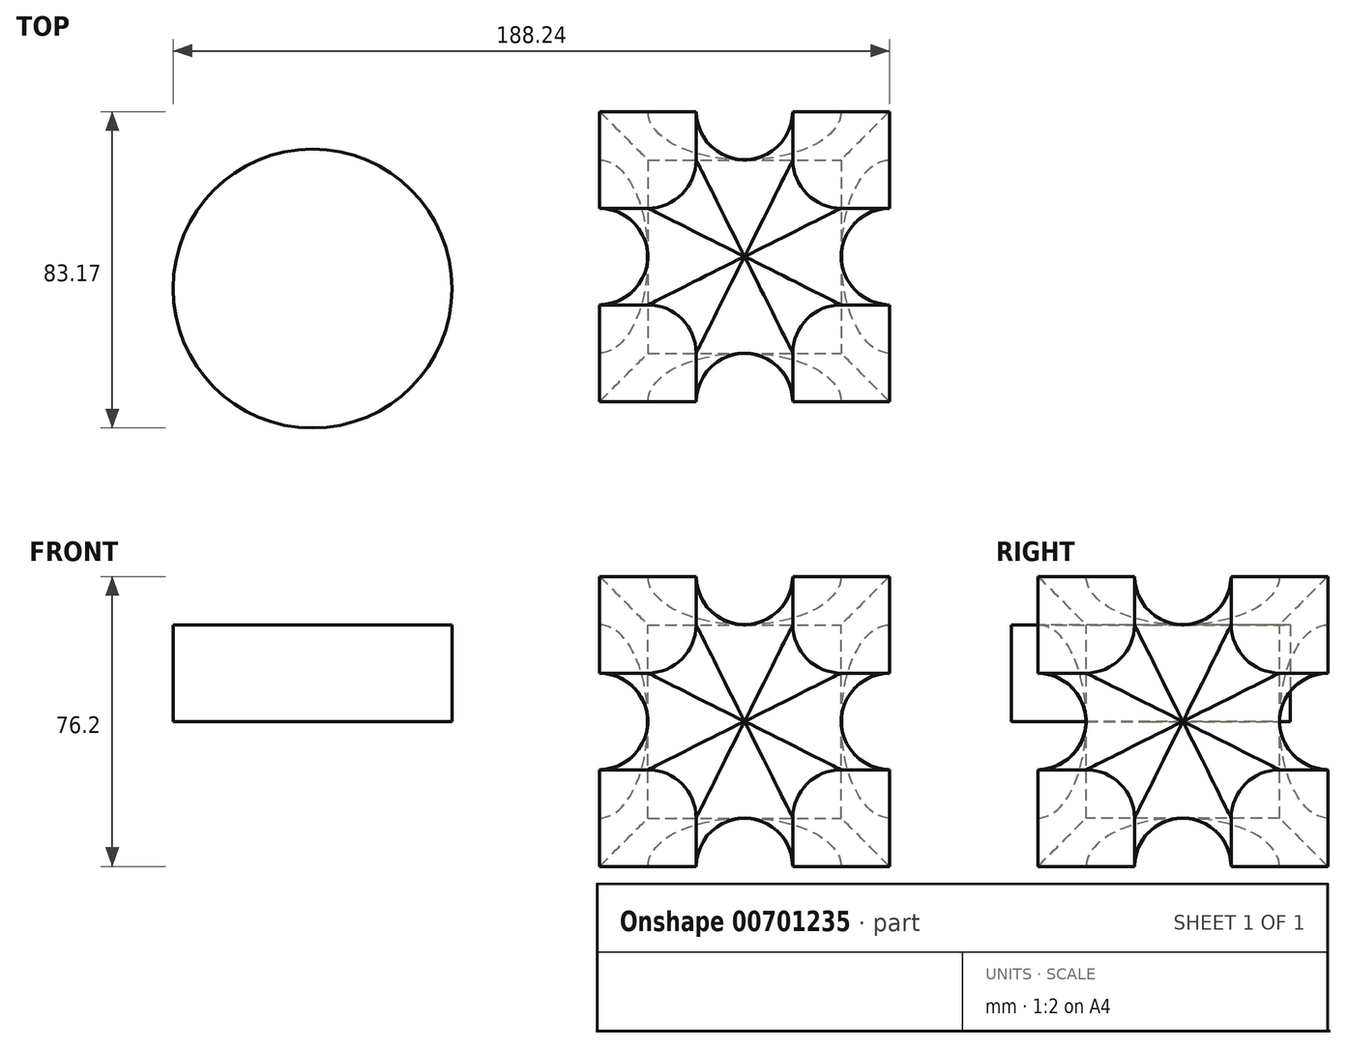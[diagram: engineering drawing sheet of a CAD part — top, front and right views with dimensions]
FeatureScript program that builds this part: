
annotation { "Feature Type Name" : "Feature", "Feature Type Description" : "" }
export const myFeature = defineFeature(function(context is Context, id is Id, definition is map)
    precondition{}
    {
        {
            var Q0;
            Q0=qCreatedBy(makeId("Top.planeOp"),FACE);
            var sketch = newSketch(context, id + "F0", { "sketchPlane" : qUnion([Q0])});
            skLineSegment(sketch, "E0.bottom", {"start": v(38.1, -38.1) * mm, "end": v(-38.1, -38.1) * mm});
            skLineSegment(sketch, "E0.top", {"start": v(38.1, 38.1) * mm, "end": v(-38.1, 38.1) * mm});
            skLineSegment(sketch, "E0.left", {"start": v(38.1, -38.1) * mm, "end": v(38.1, 38.1) * mm});
            skLineSegment(sketch, "E0.right", {"start": v(-38.1, -38.1) * mm, "end": v(-38.1, 38.1) * mm});
            skPoint(sketch, "E0.middle", {"position": v(0, 0) * mm});
            skSolve(sketch);
        }
        {
            var Q0;
            Q0 = qSketchRegion(id + "F0", true);
            extrude(context, id + "F1", {"entities" : qUnion([Q0]), "endBound" : BoundingType.SYMMETRIC, "depth" : 76.2 * mm, "offsetDistance" : 25.4 * mm});
        }
        {
            var Q0;
            Q0=makeQuery(id+"F1.opExtrude","CAP_FACE",FACE,{"disambiguationData":[OSD([sQuery(id+"F0.wireOp",EDGE,"E0.bottom"),sQuery(id+"F0.wireOp",EDGE,"E0.top"),sQuery(id+"F0.wireOp",EDGE,"E0.left"),sQuery(id+"F0.wireOp",EDGE,"E0.right")])],"isStart":false});
            var sketch = newSketch(context, id + "F2", { "sketchPlane" : qUnion([Q0])});
            skArc(sketch, "E1", {"start": v(-12.7, -38.1) * mm, "mid": v(0, -25.4) * mm, "end": v(12.7, -38.1) * mm});
            skArc(sketch, "E2", {"start": v(38.1, 12.7) * mm, "mid": v(25.4, 0) * mm, "end": v(38.1, -12.7) * mm});
            skArc(sketch, "E3", {"start": v(-12.7, 38.1) * mm, "mid": v(0, 25.4) * mm, "end": v(12.7, 38.1) * mm});
            skArc(sketch, "E4", {"start": v(-38.1, 12.7) * mm, "mid": v(-25.4, 0) * mm, "end": v(-38.1, -12.7) * mm});
            skLineSegment(sketch, "E5", {"start": v(12.7, 38.1) * mm, "end": v(-12.7, 38.1) * mm});
            skLineSegment(sketch, "E6", {"start": v(38.1, 12.7) * mm, "end": v(38.1, -12.7) * mm});
            skLineSegment(sketch, "E7", {"start": v(12.7, -38.1) * mm, "end": v(-12.7, -38.1) * mm});
            skLineSegment(sketch, "E8", {"start": v(-38.1, 12.7) * mm, "end": v(-38.1, -12.7) * mm});
            skSolve(sketch);
        }
        {
            var Q0;
            Q0=makeQuery(id+"F1.opExtrude","SWEPT_FACE",FACE,{"disambiguationData":[OSD([sQuery(id+"F0.wireOp",EDGE,"E0.bottom")])]});
            var sketch = newSketch(context, id + "F3", { "sketchPlane" : qUnion([Q0])});
            skArc(sketch, "E9", {"start": v(12.7, 38.1) * mm, "mid": v(0, 25.4) * mm, "end": v(-12.7, 38.1) * mm});
            skArc(sketch, "E10", {"start": v(38.1, 12.7) * mm, "mid": v(25.4, 0) * mm, "end": v(38.1, -12.7) * mm});
            skArc(sketch, "E11", {"start": v(12.7, -38.1) * mm, "mid": v(0, -25.4) * mm, "end": v(-12.7, -38.1) * mm});
            skArc(sketch, "E12", {"start": v(-38.1, 12.7) * mm, "mid": v(-25.4, 0) * mm, "end": v(-38.1, -12.7) * mm});
            skLineSegment(sketch, "E13", {"start": v(-12.7, 38.1) * mm, "end": v(12.7, 38.1) * mm});
            skLineSegment(sketch, "E14", {"start": v(38.1, 12.7) * mm, "end": v(38.1, -12.7) * mm});
            skLineSegment(sketch, "E15", {"start": v(12.7, -38.1) * mm, "end": v(-12.7, -38.1) * mm});
            skLineSegment(sketch, "E16", {"start": v(-38.1, -12.7) * mm, "end": v(-38.1, 12.7) * mm});
            skSolve(sketch);
        }
        {
            var Q0;
            Q0=makeQuery(id+"F1.opExtrude","SWEPT_FACE",FACE,{"disambiguationData":[OSD([sQuery(id+"F0.wireOp",EDGE,"E0.left")])]});
            var sketch = newSketch(context, id + "F4", { "sketchPlane" : qUnion([Q0])});
            skArc(sketch, "E17", {"start": v(12.7, 38.1) * mm, "mid": v(0, 25.4) * mm, "end": v(-12.7, 38.1) * mm});
            skArc(sketch, "E18", {"start": v(38.1, 12.7) * mm, "mid": v(25.4, 0) * mm, "end": v(38.1, -12.7) * mm});
            skArc(sketch, "E19", {"start": v(12.7, -38.1) * mm, "mid": v(0, -25.4) * mm, "end": v(-12.7, -38.1) * mm});
            skArc(sketch, "E20", {"start": v(-38.1, 12.7) * mm, "mid": v(-25.4, 0) * mm, "end": v(-38.1, -12.7) * mm});
            skLineSegment(sketch, "E21", {"start": v(12.7, 38.1) * mm, "end": v(-12.7, 38.1) * mm});
            skLineSegment(sketch, "E22", {"start": v(38.1, 12.7) * mm, "end": v(38.1, -12.7) * mm});
            skLineSegment(sketch, "E23", {"start": v(12.7, -38.1) * mm, "end": v(-12.7, -38.1) * mm});
            skLineSegment(sketch, "E24", {"start": v(-38.1, 12.7) * mm, "end": v(-38.1, -12.7) * mm});
            skSolve(sketch);
        }
        {
            var Q0;
            Q0 = qSketchRegion(id + "F2", true);
            extrude(context, id + "F5", {"entities" : qUnion([Q0]), "operationType" : NewBodyOperationType.REMOVE, "endBound" : BoundingType.THROUGH_ALL, "oppositeDirection" : true, "depth" : 25.4 * mm, "offsetDistance" : 25.4 * mm});
        }
        {
            var Q0;
            Q0 = qSketchRegion(id + "F3", true);
            extrude(context, id + "F6", {"entities" : qUnion([Q0]), "operationType" : NewBodyOperationType.REMOVE, "endBound" : BoundingType.THROUGH_ALL, "oppositeDirection" : true, "depth" : 25.4 * mm, "offsetDistance" : 25.4 * mm});
        }
        {
            var Q0;
            Q0 = qSketchRegion(id + "F4", true);
            extrude(context, id + "F7", {"entities" : qUnion([Q0]), "operationType" : NewBodyOperationType.REMOVE, "endBound" : BoundingType.THROUGH_ALL, "oppositeDirection" : true, "depth" : 25.4 * mm, "offsetDistance" : 25.4 * mm});
        }
        {
            var Q0;
            Q0=makeQuery(id+"F6.boolean.opBoolean","INTERSECT",EDGE,{"disambiguationData":[OD(3.0)],"derivedFrom":[makeQuery(id+"F5.boolean.opBoolean","COPY",FACE,{"derivedFrom":makeQuery(id+"F5.opExtrude","SWEPT_FACE",FACE,{"disambiguationData":[OSD([sQuery(id+"F2.wireOp",EDGE,"E2")])]})}),makeQuery(id+"F6.opExtrude","SWEPT_FACE",FACE,{"disambiguationData":[OSD([sQuery(id+"F3.wireOp",EDGE,"E10")])]})]});
            var Q1;
            Q1=makeQuery(id+"F6.boolean.opBoolean","INTERSECT",EDGE,{"disambiguationData":[OD(2.0)],"derivedFrom":[makeQuery(id+"F5.boolean.opBoolean","COPY",FACE,{"derivedFrom":makeQuery(id+"F5.opExtrude","SWEPT_FACE",FACE,{"disambiguationData":[OSD([sQuery(id+"F2.wireOp",EDGE,"E2")])]})}),makeQuery(id+"F6.opExtrude","SWEPT_FACE",FACE,{"disambiguationData":[OSD([sQuery(id+"F3.wireOp",EDGE,"E10")])]})]});
            var Q2;
            Q2=makeQuery(id+"F6.boolean.opBoolean","INTERSECT",EDGE,{"disambiguationData":[OD(0.0)],"derivedFrom":[makeQuery(id+"F5.boolean.opBoolean","COPY",FACE,{"derivedFrom":makeQuery(id+"F5.opExtrude","SWEPT_FACE",FACE,{"disambiguationData":[OSD([sQuery(id+"F2.wireOp",EDGE,"E2")])]})}),makeQuery(id+"F6.opExtrude","SWEPT_FACE",FACE,{"disambiguationData":[OSD([sQuery(id+"F3.wireOp",EDGE,"E10")])]})]});
            var Q3;
            Q3=makeQuery(id+"F6.boolean.opBoolean","INTERSECT",EDGE,{"disambiguationData":[OD(1.0)],"derivedFrom":[makeQuery(id+"F5.boolean.opBoolean","COPY",FACE,{"derivedFrom":makeQuery(id+"F5.opExtrude","SWEPT_FACE",FACE,{"disambiguationData":[OSD([sQuery(id+"F2.wireOp",EDGE,"E2")])]})}),makeQuery(id+"F6.opExtrude","SWEPT_FACE",FACE,{"disambiguationData":[OSD([sQuery(id+"F3.wireOp",EDGE,"E10")])]})]});
            var Q4;
            Q4=makeQuery(id+"F7.boolean.opBoolean","INTERSECT",EDGE,{"disambiguationData":[OD(0.0)],"derivedFrom":[makeQuery(id+"F6.boolean.opBoolean","COPY",FACE,{"derivedFrom":makeQuery(id+"F6.opExtrude","SWEPT_FACE",FACE,{"disambiguationData":[OSD([sQuery(id+"F3.wireOp",EDGE,"E11")])]})}),makeQuery(id+"F7.opExtrude","SWEPT_FACE",FACE,{"disambiguationData":[OSD([sQuery(id+"F4.wireOp",EDGE,"E19")])]})]});
            var Q5;
            Q5=makeQuery(id+"F7.boolean.opBoolean","INTERSECT",EDGE,{"disambiguationData":[OD(2.0)],"derivedFrom":[makeQuery(id+"F6.boolean.opBoolean","COPY",FACE,{"derivedFrom":makeQuery(id+"F6.opExtrude","SWEPT_FACE",FACE,{"disambiguationData":[OSD([sQuery(id+"F3.wireOp",EDGE,"E11")])]})}),makeQuery(id+"F7.opExtrude","SWEPT_FACE",FACE,{"disambiguationData":[OSD([sQuery(id+"F4.wireOp",EDGE,"E19")])]})]});
            var Q6;
            Q6=makeQuery(id+"F7.boolean.opBoolean","INTERSECT",EDGE,{"disambiguationData":[OD(3.0)],"derivedFrom":[makeQuery(id+"F6.boolean.opBoolean","COPY",FACE,{"derivedFrom":makeQuery(id+"F6.opExtrude","SWEPT_FACE",FACE,{"disambiguationData":[OSD([sQuery(id+"F3.wireOp",EDGE,"E11")])]})}),makeQuery(id+"F7.opExtrude","SWEPT_FACE",FACE,{"disambiguationData":[OSD([sQuery(id+"F4.wireOp",EDGE,"E19")])]})]});
            var Q7;
            Q7=makeQuery(id+"F7.boolean.opBoolean","INTERSECT",EDGE,{"disambiguationData":[OD(1.0)],"derivedFrom":[makeQuery(id+"F6.boolean.opBoolean","COPY",FACE,{"derivedFrom":makeQuery(id+"F6.opExtrude","SWEPT_FACE",FACE,{"disambiguationData":[OSD([sQuery(id+"F3.wireOp",EDGE,"E11")])]})}),makeQuery(id+"F7.opExtrude","SWEPT_FACE",FACE,{"disambiguationData":[OSD([sQuery(id+"F4.wireOp",EDGE,"E19")])]})]});
            var Q8;
            Q8=makeQuery(id+"F6.boolean.opBoolean","INTERSECT",EDGE,{"disambiguationData":[OD(2.0)],"derivedFrom":[makeQuery(id+"F5.boolean.opBoolean","COPY",FACE,{"derivedFrom":makeQuery(id+"F5.opExtrude","SWEPT_FACE",FACE,{"disambiguationData":[OSD([sQuery(id+"F2.wireOp",EDGE,"E4")])]})}),makeQuery(id+"F6.opExtrude","SWEPT_FACE",FACE,{"disambiguationData":[OSD([sQuery(id+"F3.wireOp",EDGE,"E12")])]})]});
            var Q9;
            Q9=makeQuery(id+"F6.boolean.opBoolean","INTERSECT",EDGE,{"disambiguationData":[OD(3.0)],"derivedFrom":[makeQuery(id+"F5.boolean.opBoolean","COPY",FACE,{"derivedFrom":makeQuery(id+"F5.opExtrude","SWEPT_FACE",FACE,{"disambiguationData":[OSD([sQuery(id+"F2.wireOp",EDGE,"E4")])]})}),makeQuery(id+"F6.opExtrude","SWEPT_FACE",FACE,{"disambiguationData":[OSD([sQuery(id+"F3.wireOp",EDGE,"E12")])]})]});
            var Q10;
            Q10=makeQuery(id+"F6.boolean.opBoolean","INTERSECT",EDGE,{"disambiguationData":[OD(1.0)],"derivedFrom":[makeQuery(id+"F5.boolean.opBoolean","COPY",FACE,{"derivedFrom":makeQuery(id+"F5.opExtrude","SWEPT_FACE",FACE,{"disambiguationData":[OSD([sQuery(id+"F2.wireOp",EDGE,"E4")])]})}),makeQuery(id+"F6.opExtrude","SWEPT_FACE",FACE,{"disambiguationData":[OSD([sQuery(id+"F3.wireOp",EDGE,"E12")])]})]});
            var Q11;
            Q11=makeQuery(id+"F6.boolean.opBoolean","INTERSECT",EDGE,{"disambiguationData":[OD(0.0)],"derivedFrom":[makeQuery(id+"F5.boolean.opBoolean","COPY",FACE,{"derivedFrom":makeQuery(id+"F5.opExtrude","SWEPT_FACE",FACE,{"disambiguationData":[OSD([sQuery(id+"F2.wireOp",EDGE,"E4")])]})}),makeQuery(id+"F6.opExtrude","SWEPT_FACE",FACE,{"disambiguationData":[OSD([sQuery(id+"F3.wireOp",EDGE,"E12")])]})]});
            var Q12;
            Q12=makeQuery(id+"F7.boolean.opBoolean","INTERSECT",EDGE,{"disambiguationData":[OD(1.0)],"derivedFrom":[makeQuery(id+"F6.boolean.opBoolean","COPY",FACE,{"derivedFrom":makeQuery(id+"F6.opExtrude","SWEPT_FACE",FACE,{"disambiguationData":[OSD([sQuery(id+"F3.wireOp",EDGE,"E9")])]})}),makeQuery(id+"F7.opExtrude","SWEPT_FACE",FACE,{"disambiguationData":[OSD([sQuery(id+"F4.wireOp",EDGE,"E17")])]})]});
            var Q13;
            Q13=makeQuery(id+"F7.boolean.opBoolean","INTERSECT",EDGE,{"disambiguationData":[OD(3.0)],"derivedFrom":[makeQuery(id+"F6.boolean.opBoolean","COPY",FACE,{"derivedFrom":makeQuery(id+"F6.opExtrude","SWEPT_FACE",FACE,{"disambiguationData":[OSD([sQuery(id+"F3.wireOp",EDGE,"E9")])]})}),makeQuery(id+"F7.opExtrude","SWEPT_FACE",FACE,{"disambiguationData":[OSD([sQuery(id+"F4.wireOp",EDGE,"E17")])]})]});
            var Q14;
            Q14=makeQuery(id+"F7.boolean.opBoolean","INTERSECT",EDGE,{"disambiguationData":[OD(2.0)],"derivedFrom":[makeQuery(id+"F6.boolean.opBoolean","COPY",FACE,{"derivedFrom":makeQuery(id+"F6.opExtrude","SWEPT_FACE",FACE,{"disambiguationData":[OSD([sQuery(id+"F3.wireOp",EDGE,"E9")])]})}),makeQuery(id+"F7.opExtrude","SWEPT_FACE",FACE,{"disambiguationData":[OSD([sQuery(id+"F4.wireOp",EDGE,"E17")])]})]});
            var Q15;
            Q15=makeQuery(id+"F7.boolean.opBoolean","INTERSECT",EDGE,{"disambiguationData":[OD(0.0)],"derivedFrom":[makeQuery(id+"F6.boolean.opBoolean","COPY",FACE,{"derivedFrom":makeQuery(id+"F6.opExtrude","SWEPT_FACE",FACE,{"disambiguationData":[OSD([sQuery(id+"F3.wireOp",EDGE,"E9")])]})}),makeQuery(id+"F7.opExtrude","SWEPT_FACE",FACE,{"disambiguationData":[OSD([sQuery(id+"F4.wireOp",EDGE,"E17")])]})]});
            var Q16;
            Q16=makeQuery(id+"F7.boolean.opBoolean","INTERSECT",EDGE,{"disambiguationData":[OD(1.0)],"derivedFrom":[makeQuery(id+"F5.boolean.opBoolean","COPY",FACE,{"derivedFrom":makeQuery(id+"F5.opExtrude","SWEPT_FACE",FACE,{"disambiguationData":[OSD([sQuery(id+"F2.wireOp",EDGE,"E1")])]})}),makeQuery(id+"F7.opExtrude","SWEPT_FACE",FACE,{"disambiguationData":[OSD([sQuery(id+"F4.wireOp",EDGE,"E20")])]})]});
            var Q17;
            Q17=makeQuery(id+"F7.boolean.opBoolean","INTERSECT",EDGE,{"disambiguationData":[OD(0.0)],"derivedFrom":[makeQuery(id+"F5.boolean.opBoolean","COPY",FACE,{"derivedFrom":makeQuery(id+"F5.opExtrude","SWEPT_FACE",FACE,{"disambiguationData":[OSD([sQuery(id+"F2.wireOp",EDGE,"E1")])]})}),makeQuery(id+"F7.opExtrude","SWEPT_FACE",FACE,{"disambiguationData":[OSD([sQuery(id+"F4.wireOp",EDGE,"E20")])]})]});
            var Q18;
            Q18=makeQuery(id+"F7.boolean.opBoolean","INTERSECT",EDGE,{"disambiguationData":[OD(2.0)],"derivedFrom":[makeQuery(id+"F5.boolean.opBoolean","COPY",FACE,{"derivedFrom":makeQuery(id+"F5.opExtrude","SWEPT_FACE",FACE,{"disambiguationData":[OSD([sQuery(id+"F2.wireOp",EDGE,"E1")])]})}),makeQuery(id+"F7.opExtrude","SWEPT_FACE",FACE,{"disambiguationData":[OSD([sQuery(id+"F4.wireOp",EDGE,"E20")])]})]});
            var Q19;
            Q19=makeQuery(id+"F7.boolean.opBoolean","INTERSECT",EDGE,{"disambiguationData":[OD(3.0)],"derivedFrom":[makeQuery(id+"F5.boolean.opBoolean","COPY",FACE,{"derivedFrom":makeQuery(id+"F5.opExtrude","SWEPT_FACE",FACE,{"disambiguationData":[OSD([sQuery(id+"F2.wireOp",EDGE,"E1")])]})}),makeQuery(id+"F7.opExtrude","SWEPT_FACE",FACE,{"disambiguationData":[OSD([sQuery(id+"F4.wireOp",EDGE,"E20")])]})]});
            var Q20;
            Q20=makeQuery(id+"F7.boolean.opBoolean","INTERSECT",EDGE,{"disambiguationData":[OD(1.0)],"derivedFrom":[makeQuery(id+"F5.boolean.opBoolean","COPY",FACE,{"derivedFrom":makeQuery(id+"F5.opExtrude","SWEPT_FACE",FACE,{"disambiguationData":[OSD([sQuery(id+"F2.wireOp",EDGE,"E3")])]})}),makeQuery(id+"F7.opExtrude","SWEPT_FACE",FACE,{"disambiguationData":[OSD([sQuery(id+"F4.wireOp",EDGE,"E18")])]})]});
            var Q21;
            Q21=makeQuery(id+"F7.boolean.opBoolean","INTERSECT",EDGE,{"disambiguationData":[OD(2.0)],"derivedFrom":[makeQuery(id+"F5.boolean.opBoolean","COPY",FACE,{"derivedFrom":makeQuery(id+"F5.opExtrude","SWEPT_FACE",FACE,{"disambiguationData":[OSD([sQuery(id+"F2.wireOp",EDGE,"E3")])]})}),makeQuery(id+"F7.opExtrude","SWEPT_FACE",FACE,{"disambiguationData":[OSD([sQuery(id+"F4.wireOp",EDGE,"E18")])]})]});
            var Q22;
            Q22=makeQuery(id+"F7.boolean.opBoolean","INTERSECT",EDGE,{"disambiguationData":[OD(3.0)],"derivedFrom":[makeQuery(id+"F5.boolean.opBoolean","COPY",FACE,{"derivedFrom":makeQuery(id+"F5.opExtrude","SWEPT_FACE",FACE,{"disambiguationData":[OSD([sQuery(id+"F2.wireOp",EDGE,"E3")])]})}),makeQuery(id+"F7.opExtrude","SWEPT_FACE",FACE,{"disambiguationData":[OSD([sQuery(id+"F4.wireOp",EDGE,"E18")])]})]});
            var Q23;
            Q23=makeQuery(id+"F7.boolean.opBoolean","INTERSECT",EDGE,{"disambiguationData":[OD(0.0)],"derivedFrom":[makeQuery(id+"F5.boolean.opBoolean","COPY",FACE,{"derivedFrom":makeQuery(id+"F5.opExtrude","SWEPT_FACE",FACE,{"disambiguationData":[OSD([sQuery(id+"F2.wireOp",EDGE,"E3")])]})}),makeQuery(id+"F7.opExtrude","SWEPT_FACE",FACE,{"disambiguationData":[OSD([sQuery(id+"F4.wireOp",EDGE,"E18")])]})]});
            fillet(context, id + "F8", {"entities" : qUnion([Q0, Q1, Q2, Q3, Q4, Q5, Q6, Q7, Q8, Q9, Q10, Q11, Q12, Q13, Q14, Q15, Q16, Q17, Q18, Q19, Q20, Q21, Q22, Q23]), "radius" : 12.7 * mm, "tangentPropagation" : true, "allowEdgeOverflow" : false});
        }
        {
            var Q0;
            Q0=qCreatedBy(makeId("Top.planeOp"),FACE);
            var sketch = newSketch(context, id + "F9", { "sketchPlane" : qUnion([Q0])});
            skCircle(sketch, "E25", {"center": v(-113.5, -8.43) * mm, "radius": 36.65 * mm});
            skSolve(sketch);
        }
        {
            var Q0;
            Q0 = qSketchRegion(id + "F9", true);
            extrude(context, id + "F10", {"entities" : qUnion([Q0]), "depth" : 25.4 * mm, "offsetDistance" : 25.4 * mm});
        }
    });
